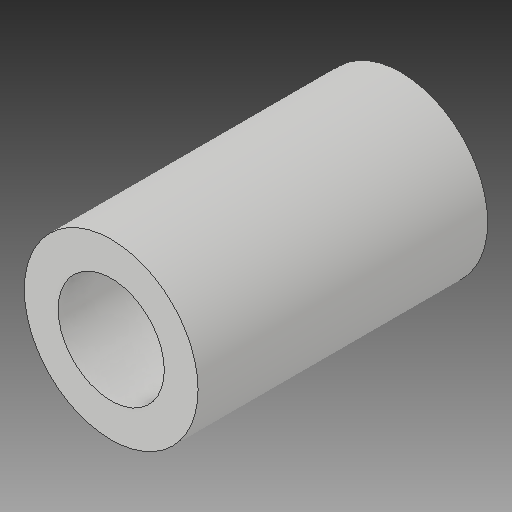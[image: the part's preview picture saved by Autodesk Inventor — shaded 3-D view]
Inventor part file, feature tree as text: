
AUTODESK INVENTOR PART (.ipt)
format: ipt  version: 2018 (Build 220112000, 112)  size: 104,960 bytes
history: native  units: mm
features: other x3, extrude x1, sketch x1, reference x1
ambient origin geometry x8: Origin, YZ Plane, XZ Plane, XY Plane, X Axis, Y Axis, Z Axis, Center Point
bodies: Solid1 (feature_tree)
feature tree (6):
  extrude  "Extrusion1"  Depth=15.0mm
  sketch  "Sketch1"  dims[d0=5.5mm d1=9.0mm d2=15.0mm d3=0.0mm]
  reference  "Reference1"
  other  "Assembly3"
  other  "Delrin Wheel:1"
  other  "SKF 625:1"
